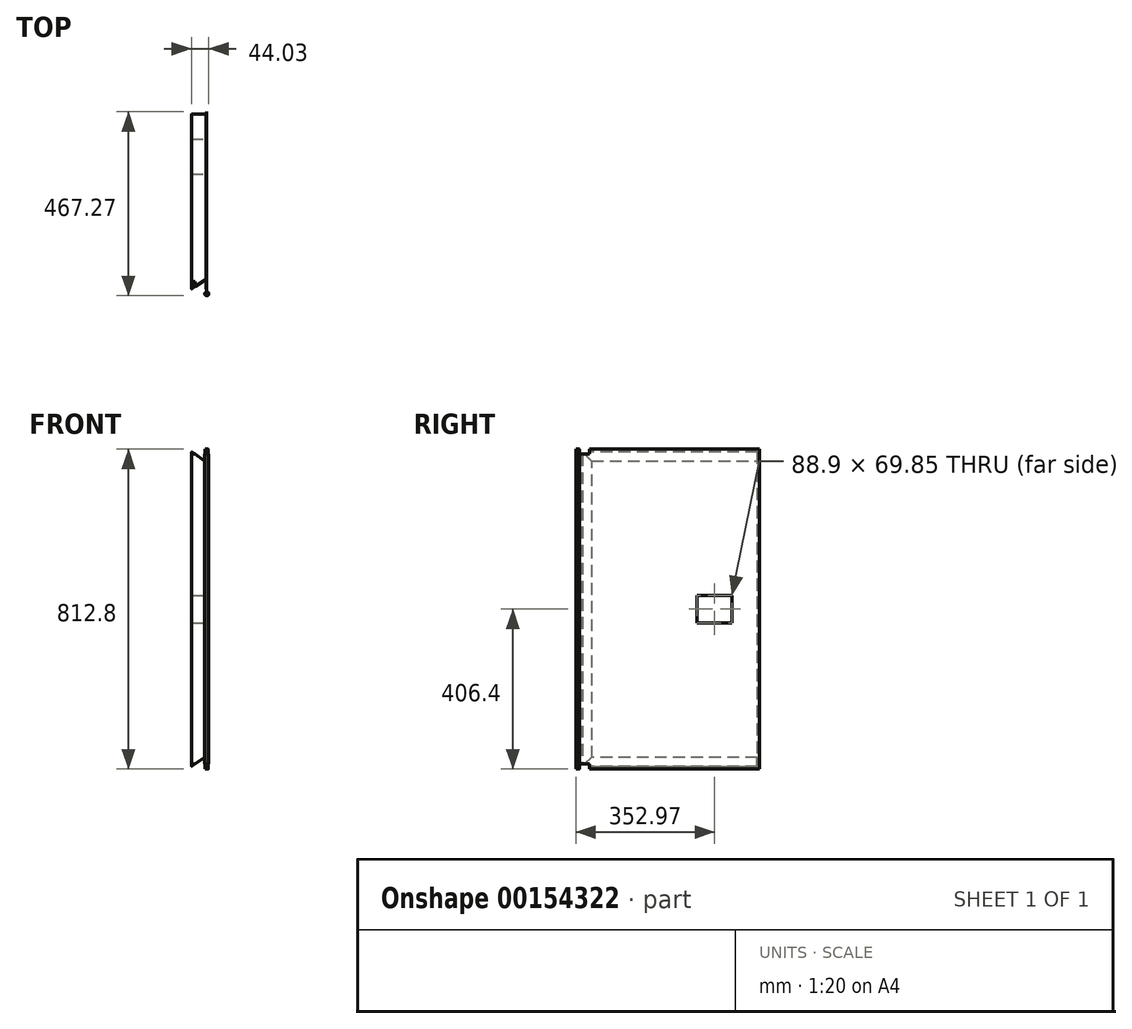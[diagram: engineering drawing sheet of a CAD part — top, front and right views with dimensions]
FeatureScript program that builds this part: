
annotation { "Feature Type Name" : "Feature", "Feature Type Description" : "" }
export const myFeature = defineFeature(function(context is Context, id is Id, definition is map)
    precondition{}
    {
        {
            var Q0;
            Q0=qCreatedBy(makeId("Right.planeOp"),FACE);
            var sketch = newSketch(context, id + "F0", { "sketchPlane" : qUnion([Q0])});
            skLineSegment(sketch, "E0.bottom", {"start": v(-203.2, 406.4) * mm, "end": v(228.6, 406.4) * mm});
            skLineSegment(sketch, "E0.left", {"start": v(-228.6, 393.7) * mm, "end": v(-228.6, -393.7) * mm});
            skLineSegment(sketch, "E0.right", {"start": v(228.6, 406.4) * mm, "end": v(228.6, -406.4) * mm});
            skPoint(sketch, "E0.middle", {"position": v(0, 0) * mm});
            skLineSegment(sketch, "E1", {"start": v(-228.6, 393.7) * mm, "end": v(-203.2, 393.7) * mm});
            skLineSegment(sketch, "E2", {"start": v(-203.2, 393.7) * mm, "end": v(-203.2, 406.4) * mm});
            skLineSegment(sketch, "E3", {"start": v(228.6, -406.4) * mm, "end": v(-203.2, -406.4) * mm});
            skLineSegment(sketch, "E4", {"start": v(-203.2, -406.4) * mm, "end": v(-203.2, -393.7) * mm});
            skLineSegment(sketch, "E5", {"start": v(-203.2, -393.7) * mm, "end": v(-228.6, -393.7) * mm});
            skLineSegment(sketch, "E6", {"start": v(-228.6, 0) * mm, "end": v(228.6, 0) * mm});
            skSolve(sketch);
        }
        {
            var Q0;
            Q0=qSketchRegion(id+"F0",true);
            extrude(context, id + "F1", {"entities" : qUnion([Q0]), "oppositeDirection" : true, "depth" : 0.89 * mm});
        }
        {
            var Q0;
            Q0=makeQuery(id+"F1.opExtrude","CAP_FACE",FACE,{"disambiguationData":[OSD([sQuery(id+"F0.wireOp",EDGE,"E0.bottom"),sQuery(id+"F0.wireOp",EDGE,"E0.top"),sQuery(id+"F0.wireOp",EDGE,"E0.left"),sQuery(id+"F0.wireOp",EDGE,"E0.right")])],"isStart":false});
            var sketch = newSketch(context, id + "F2", { "sketchPlane" : qUnion([Q0])});
            skLineSegment(sketch, "E7.bottom", {"start": v(-222.25, 400.05) * mm, "end": v(203.2, 400.05) * mm});
            skLineSegment(sketch, "E7.top", {"start": v(-222.25, -400.05) * mm, "end": v(203.2, -400.05) * mm});
            skLineSegment(sketch, "E7.left", {"start": v(-222.25, 400.05) * mm, "end": v(-222.25, -400.05) * mm});
            skLineSegment(sketch, "E7.right", {"start": v(222.25, 393.7) * mm, "end": v(222.25, -393.7) * mm});
            skPoint(sketch, "E7.middle", {"position": v(0, 0) * mm});
            skLineSegment(sketch, "E8", {"start": v(222.25, 393.7) * mm, "end": v(203.2, 393.7) * mm});
            skLineSegment(sketch, "E9", {"start": v(203.2, 393.7) * mm, "end": v(203.2, 400.05) * mm});
            skLineSegment(sketch, "E10", {"start": v(222.25, -393.7) * mm, "end": v(203.2, -393.7) * mm});
            skLineSegment(sketch, "E11", {"start": v(203.2, -393.7) * mm, "end": v(203.2, -400.05) * mm});
            skSolve(sketch);
        }
        {
            var Q0;
            Q0=qSketchRegion(id+"F2",true);
            extrude(context, id + "F3", {"entities" : qUnion([Q0]), "operationType" : NewBodyOperationType.ADD, "depth" : 38.1 * mm});
        }
        {
            var Q0;
            Q0=makeQuery(id+"F3.opExtrude","SWEPT_FACE",FACE,{"disambiguationData":[OSD([sQuery(id+"F2.wireOp",EDGE,"E7.left")])]});
            var sketch = newSketch(context, id + "F4", { "sketchPlane" : qUnion([Q0])});
            skLineSegment(sketch, "E12", {"start": v(38.99, 400.05) * mm, "end": v(38.99, -400.05) * mm});
            skLineSegment(sketch, "E13", {"start": v(38.99, 400.05) * mm, "end": v(2.13, 375.2) * mm});
            skLineSegment(sketch, "E14", {"start": v(2.13, 400.05) * mm, "end": v(2.13, -400.05) * mm});
            skLineSegment(sketch, "E15", {"start": v(38.99, -400.05) * mm, "end": v(2.13, -375.2) * mm});
            skSolve(sketch);
        }
        {
            var Q0;
            {var subQ3=sQuery(id+"F4.wireOp",EDGE,"E15");Q0=makeQuery(id+"F4.imprint","IMPRINT",FACE,{"disambiguationData":[TD([[makeQuery(id+"F4.imprint","IMPRINT",EDGE,{"derivedFrom":subQ3}),1.0]])]});}
            var Q1;
            {var subQ0=sQuery(id+"F4.wireOp",EDGE,"E13");Q1=makeQuery(id+"F4.imprint","IMPRINT",FACE,{"disambiguationData":[TD([[makeQuery(id+"F4.imprint","IMPRINT",EDGE,{"derivedFrom":subQ0}),-1.0]])]});}
            extrude(context, id + "F5", {"entities" : qUnion([Q0, Q1]), "operationType" : NewBodyOperationType.REMOVE, "endBound" : BoundingType.THROUGH_ALL, "oppositeDirection" : true, "depth" : 25.4 * mm});
        }
        {
            var Q0;
            {var subQ0=sQuery(id+"F4.wireOp",EDGE,"E14");var subQ2=sQuery(id+"F2.wireOp",EDGE,"E7.bottom");Q0=makeQuery(id+"F5.boolean.opBoolean","SPLIT",FACE,{"disambiguationData":[TD([makeQuery(id+"F5.opExtrude","SWEPT_FACE",FACE,{"disambiguationData":[OSD([subQ0]),TDD([makeQuery(id+"F4.imprint","IMPRINT",EDGE,{"disambiguationData":[TD([[makeQuery(id+"F4.imprint","INTERSECT",VERTEX,{"derivedFrom":[sQuery(id+"F4.wireOp",EDGE,"E13"),subQ0]}),1.0]])],"derivedFrom":subQ0})])]})])],"derivedFrom":makeQuery(id+"F3.opExtrude","SWEPT_FACE",FACE,{"disambiguationData":[OSD([subQ2])]})});}
            var sketch = newSketch(context, id + "F6", { "sketchPlane" : qUnion([Q0])});
            skLineSegment(sketch, "E16", {"start": v(-38.99, 222.25) * mm, "end": v(-2.13, 247.1) * mm});
            skLineSegment(sketch, "E17", {"start": v(-38.99, 222.25) * mm, "end": v(-2.13, 222.25) * mm});
            skLineSegment(sketch, "E18", {"start": v(-2.13, 222.25) * mm, "end": v(-2.13, 247.1) * mm});
            skLineSegment(sketch, "E19", {"start": v(-2.13, -197.4) * mm, "end": v(-2.13, -222.25) * mm});
            skLineSegment(sketch, "E20", {"start": v(-2.13, -222.25) * mm, "end": v(-38.99, -222.25) * mm});
            skLineSegment(sketch, "E21", {"start": v(-38.99, -222.25) * mm, "end": v(-2.13, -197.4) * mm});
            skSolve(sketch);
        }
        {
            var Q0;
            Q0=makeQuery(id+"F6.imprint","IMPRINT",FACE,{"disambiguationData":[TD([[makeQuery(id+"F6.imprint","IMPRINT",EDGE,{"derivedFrom":sQuery(id+"F6.wireOp",EDGE,"E16")}),1.0]])]});
            var Q1;
            {var subQ3=sQuery(id+"F6.wireOp",EDGE,"E20");Q1=makeQuery(id+"F6.imprint","IMPRINT",FACE,{"disambiguationData":[TD([[makeQuery(id+"F6.imprint","IMPRINT",EDGE,{"derivedFrom":subQ3}),-1.0]])]});}
            extrude(context, id + "F7", {"entities" : qUnion([Q0, Q1]), "operationType" : NewBodyOperationType.REMOVE, "endBound" : BoundingType.THROUGH_ALL, "oppositeDirection" : true, "depth" : 25.4 * mm});
        }
        {
            var Q0;
            Q0=makeQuery(id+"F3.opExtrude","CAP_EDGE",EDGE,{"disambiguationData":[OSD([sQuery(id+"F2.wireOp",EDGE,"E7.top")])],"isStart":false});
            var Q1;
            Q1=makeQuery(id+"F3.opExtrude","CAP_EDGE",EDGE,{"disambiguationData":[OSD([sQuery(id+"F2.wireOp",EDGE,"E7.left")])],"isStart":false});
            var Q2;
            Q2=makeQuery(id+"F3.opExtrude","CAP_EDGE",EDGE,{"disambiguationData":[OSD([sQuery(id+"F2.wireOp",EDGE,"E7.bottom")])],"isStart":false});
            var Q3;
            Q3=makeQuery(id+"F3.opExtrude","CAP_EDGE",EDGE,{"disambiguationData":[OSD([sQuery(id+"F2.wireOp",EDGE,"E7.right")])],"isStart":false});
            fillet(context, id + "F8", {"entities" : qUnion([Q0, Q1, Q2, Q3]), "radius" : 1.27 * mm, "tangentPropagation" : true, "allowEdgeOverflow" : false});
        }
        {
            var Q0;
            Q0=makeQuery(id+"F7.boolean.opBoolean","COPY",EDGE,{"derivedFrom":makeQuery(id+"F7.opExtrude","SWEPT_EDGE",EDGE,{"disambiguationData":[OSD([sQuery(id+"F6.wireOp",EDGE,"9kJs9u86-Rynm-MJaU-KLCn-ISIbLXFeB2s4"),sQuery(id+"F6.wireOp",EDGE,"E16")])]})});
            var Q1;
            Q1=makeQuery(id+"F5.boolean.opBoolean","COPY",EDGE,{"derivedFrom":makeQuery(id+"F5.opExtrude","SWEPT_EDGE",EDGE,{"disambiguationData":[OSD([sQuery(id+"F4.wireOp",EDGE,"E13"),sQuery(id+"F4.wireOp",EDGE,"E14")])]})});
            var Q2;
            Q2=makeQuery(id+"F7.boolean.opBoolean","COPY",EDGE,{"derivedFrom":makeQuery(id+"F7.opExtrude","SWEPT_EDGE",EDGE,{"disambiguationData":[OSD([sQuery(id+"F6.wireOp",EDGE,"9kJs9u86-Rynm-MJaU-KLCn-ISIbLXFeB2s4"),sQuery(id+"F6.wireOp",EDGE,"E16")])]})});
            var Q3;
            Q3=makeQuery(id+"F5.boolean.opBoolean","COPY",EDGE,{"derivedFrom":makeQuery(id+"F5.opExtrude","SWEPT_EDGE",EDGE,{"disambiguationData":[OSD([sQuery(id+"F4.wireOp",EDGE,"E14"),sQuery(id+"F4.wireOp",EDGE,"E15")])]})});
            fillet(context, id + "F9", {"entities" : qUnion([Q0, Q1, Q2, Q3]), "radius" : 1.27 * mm, "tangentPropagation" : true, "allowEdgeOverflow" : false});
        }
        {
            var Q0;
            Q0=makeQuery(id+"F1.opExtrude","CAP_FACE",FACE,{"disambiguationData":[OSD([sQuery(id+"F0.wireOp",EDGE,"E0.bottom"),sQuery(id+"F0.wireOp",EDGE,"E0.top"),sQuery(id+"F0.wireOp",EDGE,"E0.left"),sQuery(id+"F0.wireOp",EDGE,"E0.right")])],"isStart":true});
            var sketch = newSketch(context, id + "F10", { "sketchPlane" : qUnion([Q0])});
            skLineSegment(sketch, "E22", {"start": v(-228.6, 0) * mm, "end": v(228.6, 0) * mm});
            skLineSegment(sketch, "E23.bottom", {"start": v(69.85, 34.93) * mm, "end": v(158.75, 34.93) * mm});
            skLineSegment(sketch, "E23.top", {"start": v(69.85, -34.92) * mm, "end": v(158.75, -34.92) * mm});
            skLineSegment(sketch, "E23.left", {"start": v(69.85, 34.93) * mm, "end": v(69.85, -34.92) * mm});
            skLineSegment(sketch, "E23.right", {"start": v(158.75, 34.93) * mm, "end": v(158.75, -34.92) * mm});
            skPoint(sketch, "E23.middle", {"position": v(114.3, 0) * mm});
            skSolve(sketch);
        }
        {
            var Q0;
            Q0=qSketchRegion(id+"F10",true);
            extrude(context, id + "F11", {"entities" : qUnion([Q0]), "operationType" : NewBodyOperationType.REMOVE, "endBound" : BoundingType.THROUGH_ALL, "oppositeDirection" : true, "depth" : 25.4 * mm});
        }
        {
            var Q0;
            Q0=qCreatedBy(makeId("Top.planeOp"),FACE);
            var sketch = newSketch(context, id + "F12", { "sketchPlane" : qUnion([Q0])});
            skCircle(sketch, "E24", {"center": v(0, -233.64) * mm, "radius": 5.04 * mm});
            skCircle(sketch, "E25", {"center": v(0, -233.64) * mm, "radius": 3.97 * mm});
            skSolve(sketch);
        }
        {
            var Q0;
            Q0=qSketchRegion(id+"F12",true);
            var Q1;
            Q1=makeQuery(id+"F3.boolean.opBoolean","MERGE",FACE,{"derivedFrom":[makeQuery(id+"F1.opExtrude","SWEPT_FACE",FACE,{"disambiguationData":[OSD([sQuery(id+"F0.wireOp",EDGE,"E1")])]}),makeQuery(id+"F3.opExtrude","SWEPT_FACE",FACE,{"disambiguationData":[OSD([sQuery(id+"F2.wireOp",EDGE,"E7.bottom")])]})]});
            var Q2;
            Q2=makeQuery(id+"F3.boolean.opBoolean","MERGE",FACE,{"derivedFrom":[makeQuery(id+"F1.opExtrude","SWEPT_FACE",FACE,{"disambiguationData":[OSD([sQuery(id+"F0.wireOp",EDGE,"E5")])]}),makeQuery(id+"F3.opExtrude","SWEPT_FACE",FACE,{"disambiguationData":[OSD([sQuery(id+"F2.wireOp",EDGE,"E7.top")])]})]});
            extrude(context, id + "F13", {"entities" : qUnion([Q0]), "endBound" : BoundingType.UP_TO_SURFACE, "endBoundEntityFace" : qUnion([Q1]), "depth" : 25.4 * mm, "hasSecondDirection" : true, "secondDirectionBound" : SecondDirectionBoundingType.UP_TO_SURFACE, "secondDirectionOppositeDirection" : true, "secondDirectionBoundEntityFace" : qUnion([Q2]), "secondDirectionDepth" : 25.4 * mm});
        }
        {
            var Q0;
            Q0=qCreatedBy(makeId("Top.planeOp"),FACE);
            var sketch = newSketch(context, id + "F14", { "sketchPlane" : qUnion([Q0])});
            skCircle(sketch, "E26", {"center": v(0, -233.64) * mm, "radius": 3.97 * mm});
            skSolve(sketch);
        }
        {
            var Q0;
            Q0=qSketchRegion(id+"F14",true);
            var Q1;
            Q1=makeQuery(id+"F1.opExtrude","SWEPT_FACE",FACE,{"disambiguationData":[OSD([sQuery(id+"F0.wireOp",EDGE,"E0.bottom")])]});
            var Q2;
            Q2=makeQuery(id+"F1.opExtrude","SWEPT_FACE",FACE,{"disambiguationData":[OSD([sQuery(id+"F0.wireOp",EDGE,"E3")])]});
            extrude(context, id + "F15", {"entities" : qUnion([Q0]), "operationType" : NewBodyOperationType.ADD, "endBound" : BoundingType.UP_TO_SURFACE, "endBoundEntityFace" : qUnion([Q1]), "depth" : 25.4 * mm, "hasSecondDirection" : true, "secondDirectionBound" : SecondDirectionBoundingType.UP_TO_SURFACE, "secondDirectionOppositeDirection" : true, "secondDirectionBoundEntityFace" : qUnion([Q2]), "secondDirectionDepth" : 25.4 * mm});
        }
    });
